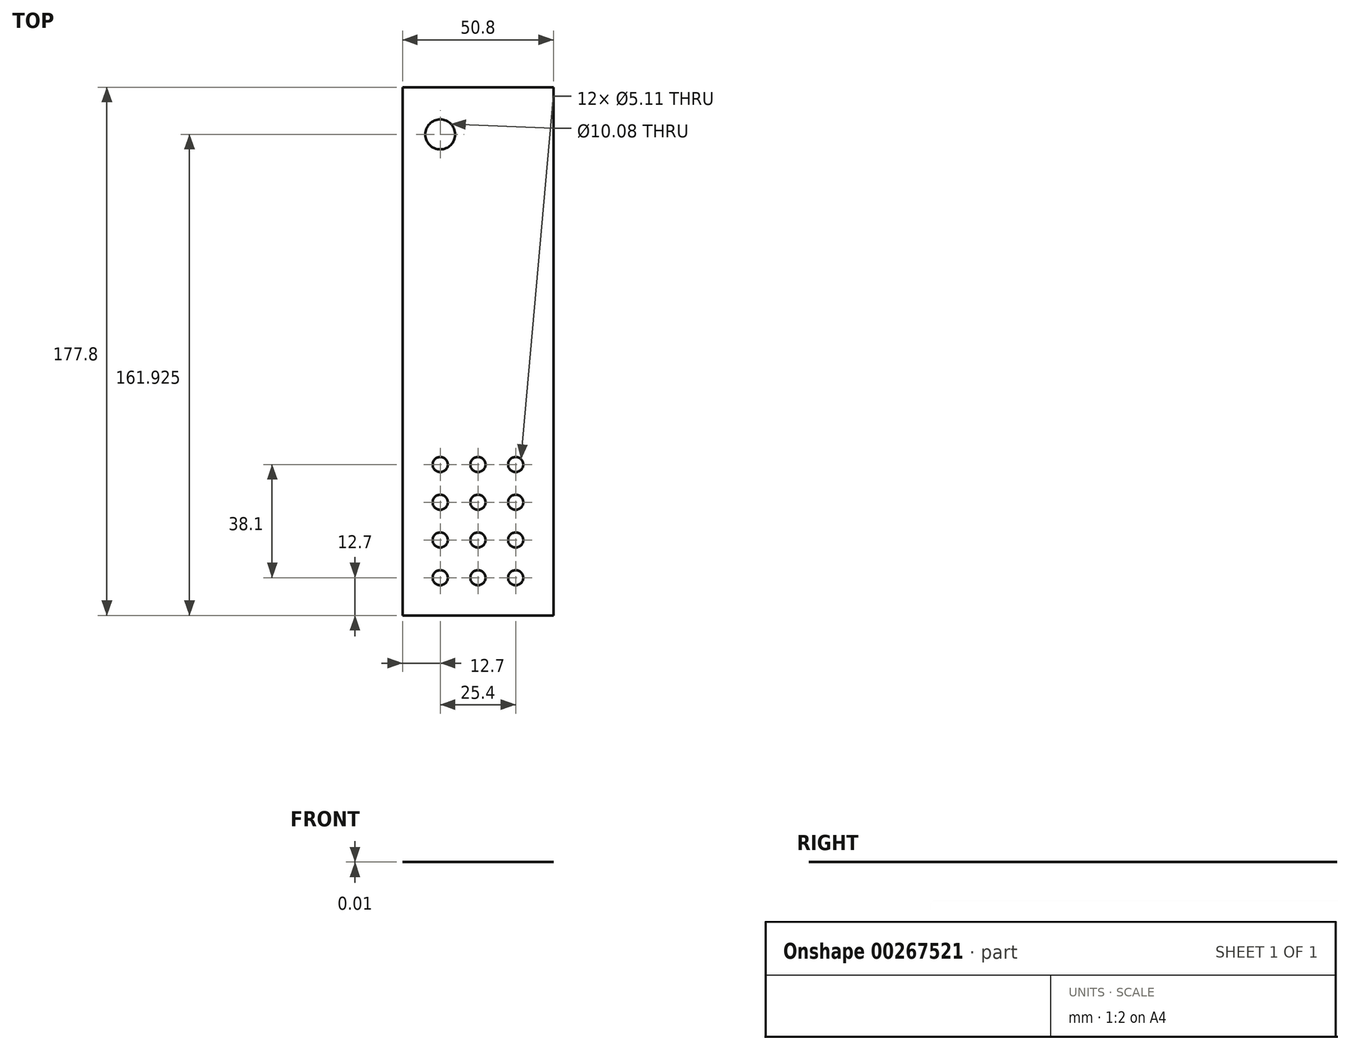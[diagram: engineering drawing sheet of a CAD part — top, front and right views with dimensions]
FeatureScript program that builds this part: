
annotation { "Feature Type Name" : "Feature", "Feature Type Description" : "" }
export const myFeature = defineFeature(function(context is Context, id is Id, definition is map)
    precondition{}
    {
        {
            var Q0;
            Q0=qCreatedBy(makeId("Top.planeOp"),FACE);
            var sketch = newSketch(context, id + "F0", { "sketchPlane" : qUnion([Q0])});
            skLineSegment(sketch, "E0.bottom", {"start": v(-50.8, 177.8) * mm, "end": v(0, 177.8) * mm});
            skLineSegment(sketch, "E0.top", {"start": v(-50.8, 0) * mm, "end": v(0, 0) * mm});
            skLineSegment(sketch, "E0.left", {"start": v(-50.8, 177.8) * mm, "end": v(-50.8, 0) * mm});
            skLineSegment(sketch, "E0.right", {"start": v(0, 177.8) * mm, "end": v(0, 0) * mm});
            skPoint(sketch, "E1", {"position": v(-12.7, 12.7) * mm});
            skPoint(sketch, "E2.0.1.0", {"position": v(-12.7, 25.4) * mm});
            skPoint(sketch, "E2.0.2.0", {"position": v(-12.7, 38.1) * mm});
            skPoint(sketch, "E2.1.0.0", {"position": v(-25.4, 12.7) * mm});
            skPoint(sketch, "E2.1.1.0", {"position": v(-25.4, 25.4) * mm});
            skPoint(sketch, "E2.1.2.0", {"position": v(-25.4, 38.1) * mm});
            skPoint(sketch, "E2.2.0.0", {"position": v(-38.1, 12.7) * mm});
            skPoint(sketch, "E2.2.1.0", {"position": v(-38.1, 25.4) * mm});
            skPoint(sketch, "E2.2.2.0", {"position": v(-38.1, 38.1) * mm});
            skLineSegment(sketch, "E2.direction1", {"start": v(-12.7, 12.7) * mm, "end": v(-25.4, 12.7) * mm, "construction": true});
            skLineSegment(sketch, "E2.direction2", {"start": v(-12.7, 12.7) * mm, "end": v(-12.7, 25.4) * mm, "construction": true});
            skPoint(sketch, "E3.0.0.3", {"position": v(-12.7, 50.8) * mm});
            skPoint(sketch, "E3.0.1.3", {"position": v(-25.4, 50.8) * mm});
            skPoint(sketch, "E3.0.2.3", {"position": v(-38.1, 50.8) * mm});
            skPoint(sketch, "E4", {"position": v(-38.1, 161.93) * mm});
            skSolve(sketch);
        }
        {
            var Q0;
            Q0=makeQuery(id+"F0.imprint","IMPRINT",FACE,{"disambiguationData":[TD([[makeQuery(id+"F0.imprint","IMPRINT",EDGE,{"derivedFrom":sQuery(id+"F0.wireOp",EDGE,"E0.bottom")}),-1.0]])]});
            extrude(context, id + "F1", {"entities" : qUnion([Q0]), "oppositeDirection" : true, "depth" : 3 / 203.2 * mm});
        }
        {
            var Q0;
            Q0=sQuery(id+"F0.wireOp",VERTEX,"E1");
            var Q1;
            Q1=sQuery(id+"F0.wireOp",VERTEX,"E2.1.0.0");
            var Q2;
            Q2=sQuery(id+"F0.wireOp",VERTEX,"E2.2.0.0");
            var Q3;
            Q3=sQuery(id+"F0.wireOp",VERTEX,"E2.2.1.0");
            var Q4;
            Q4=sQuery(id+"F0.wireOp",VERTEX,"E2.1.1.0");
            var Q5;
            Q5=sQuery(id+"F0.wireOp",VERTEX,"E2.0.1.0");
            var Q6;
            Q6=sQuery(id+"F0.wireOp",VERTEX,"E2.0.2.0");
            var Q7;
            Q7=sQuery(id+"F0.wireOp",VERTEX,"E2.1.2.0");
            var Q8;
            Q8=sQuery(id+"F0.wireOp",VERTEX,"E2.2.2.0");
            var Q9;
            Q9=sQuery(id+"F0.wireOp",VERTEX,"E3.0.2.3");
            var Q10;
            Q10=sQuery(id+"F0.wireOp",VERTEX,"E3.0.1.3");
            var Q11;
            Q11=sQuery(id+"F0.wireOp",VERTEX,"E3.0.0.3");
            var Q12;
            Q12=makeQuery(id+"F1.opExtrude","SWEPT_BODY",BODY,{"disambiguationData":[OSD([sQuery(id+"F0.wireOp",EDGE,"E0.bottom"),sQuery(id+"F0.wireOp",EDGE,"E0.top"),sQuery(id+"F0.wireOp",EDGE,"E0.left"),sQuery(id+"F0.wireOp",EDGE,"E0.right")])]});
            hole(context, id + "F2", {"style" : HoleStyle.SIMPLE, "endStyle" : HoleEndStyle.THROUGH, "standardTappedOrClearance" : lookupTablePath({ "standard" : "ANSI", "engagement" : "75%", "pitch" : "20 tpi", "size" : "1/4", "type" : "Tapped" }), "standardBlindInLast" : lookupTablePath({ "standard" : "ANSI", "engagement" : "75%", "pitch" : "20 tpi", "size" : "1/4", "type" : "Tapped" }), "holeDiameter" : 5.1 * mm, "showTappedDepth" : true, "tappedDepth" : 12.7 * mm, "tapClearance" : 3, "startFromSketch" : true, "locations" : qUnion([Q0, Q1, Q2, Q3, Q4, Q5, Q6, Q7, Q8, Q9, Q10, Q11]), "scope" : qUnion([Q12]), "majorDiameter" : 6.35 * mm});
        }
        {
            var Q0;
            Q0=sQuery(id+"F0.wireOp",VERTEX,"E4");
            var Q1;
            Q1=makeQuery(id+"F1.opExtrude","SWEPT_BODY",BODY,{"disambiguationData":[OSD([sQuery(id+"F0.wireOp",EDGE,"E0.bottom"),sQuery(id+"F0.wireOp",EDGE,"E0.top"),sQuery(id+"F0.wireOp",EDGE,"E0.left"),sQuery(id+"F0.wireOp",EDGE,"E0.right")])]});
            hole(context, id + "F3", {"style" : HoleStyle.SIMPLE, "endStyle" : HoleEndStyle.THROUGH, "standardTappedOrClearance" : lookupTablePath({ "standard" : "ANSI", "fit" : "Normal (ASME)", "size" : "3/8", "type" : "Clearance" }), "standardBlindInLast" : lookupTablePath({ "fit" : "Free", "standard" : "ANSI", "size" : "3/8", "type" : "Clearance" }), "holeDiameter" : 10.08 * mm, "tappedDepth" : 12.7 * mm, "tapClearance" : 3, "startFromSketch" : true, "locations" : qUnion([Q0]), "scope" : qUnion([Q1])});
        }
    });
